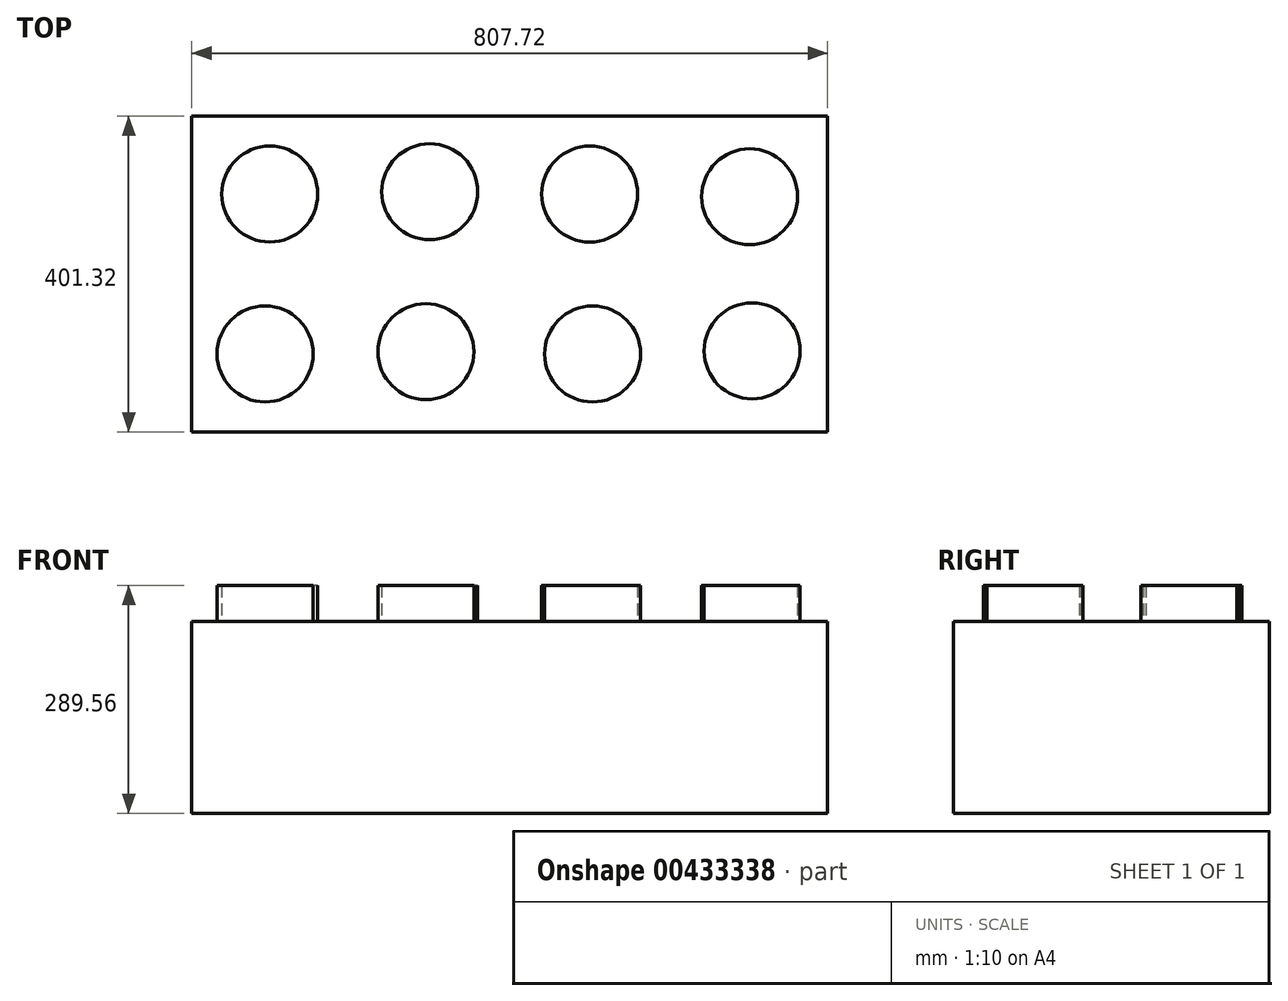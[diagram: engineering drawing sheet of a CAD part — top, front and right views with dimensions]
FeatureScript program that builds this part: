
annotation { "Feature Type Name" : "Feature", "Feature Type Description" : "" }
export const myFeature = defineFeature(function(context is Context, id is Id, definition is map)
    precondition{}
    {
        {
            var Q0;
            Q0=qCreatedBy(makeId("Top.planeOp"),FACE);
            var sketch = newSketch(context, id + "F0", { "sketchPlane" : qUnion([Q0])});
            skLineSegment(sketch, "E0.bottom", {"start": v(-391.6, 82.43) * mm, "end": v(416.12, 82.43) * mm});
            skLineSegment(sketch, "E0.top", {"start": v(-391.6, -318.9) * mm, "end": v(416.12, -318.9) * mm});
            skLineSegment(sketch, "E0.left", {"start": v(-391.6, 82.43) * mm, "end": v(-391.6, -318.9) * mm});
            skLineSegment(sketch, "E0.right", {"start": v(416.12, 82.43) * mm, "end": v(416.12, -318.9) * mm});
            skSolve(sketch);
        }
        {
            var Q0;
            Q0 = qSketchRegion(id + "F0", true);
            extrude(context, id + "F1", {"entities" : qUnion([Q0]), "depth" : 243.84 * mm});
        }
        {
            var Q0;
            Q0=makeQuery(id+"F1.opExtrude","CAP_FACE",FACE,{"disambiguationData":[OSD([sQuery(id+"F0.wireOp",EDGE,"E0.bottom"),sQuery(id+"F0.wireOp",EDGE,"E0.top"),sQuery(id+"F0.wireOp",EDGE,"E0.left"),sQuery(id+"F0.wireOp",EDGE,"E0.right")])],"isStart":false});
            var sketch = newSketch(context, id + "F2", { "sketchPlane" : qUnion([Q0])});
            skCircle(sketch, "E1", {"center": v(-292.54, -16.63) * mm, "radius": 60.96 * mm});
            skCircle(sketch, "E2", {"center": v(-89.34, -13.7) * mm, "radius": 60.96 * mm});
            skCircle(sketch, "E3", {"center": v(113.84, -16.64) * mm, "radius": 60.96 * mm});
            skCircle(sketch, "E4", {"center": v(317.01, -19.95) * mm, "radius": 60.96 * mm});
            skCircle(sketch, "E5", {"center": v(-298.57, -219.74) * mm, "radius": 60.96 * mm});
            skCircle(sketch, "E6", {"center": v(-94.25, -216.9) * mm, "radius": 60.96 * mm});
            skCircle(sketch, "E7", {"center": v(117.44, -219.8) * mm, "radius": 60.96 * mm});
            skCircle(sketch, "E8", {"center": v(320.06, -215.88) * mm, "radius": 60.96 * mm});
            skSolve(sketch);
        }
        {
            var Q0;
            Q0=makeQuery(id+"F2.imprint","IMPRINT",FACE,{"disambiguationData":[TD([[makeQuery(id+"F2.imprint","IMPRINT",EDGE,{"derivedFrom":sQuery(id+"F2.wireOp",EDGE,"E3")}),1.0]])]});
            var Q1;
            Q1=makeQuery(id+"F2.imprint","IMPRINT",FACE,{"disambiguationData":[TD([[makeQuery(id+"F2.imprint","IMPRINT",EDGE,{"derivedFrom":sQuery(id+"F2.wireOp",EDGE,"E4")}),1.0]])]});
            var Q2;
            Q2=makeQuery(id+"F2.imprint","IMPRINT",FACE,{"disambiguationData":[TD([[makeQuery(id+"F2.imprint","IMPRINT",EDGE,{"derivedFrom":sQuery(id+"F2.wireOp",EDGE,"E5")}),1.0]])]});
            var Q3;
            Q3=makeQuery(id+"F2.imprint","IMPRINT",FACE,{"disambiguationData":[TD([[makeQuery(id+"F2.imprint","IMPRINT",EDGE,{"derivedFrom":sQuery(id+"F2.wireOp",EDGE,"E6")}),1.0]])]});
            var Q4;
            Q4=makeQuery(id+"F2.imprint","IMPRINT",FACE,{"disambiguationData":[TD([[makeQuery(id+"F2.imprint","IMPRINT",EDGE,{"derivedFrom":sQuery(id+"F2.wireOp",EDGE,"E7")}),1.0]])]});
            var Q5;
            Q5=makeQuery(id+"F2.imprint","IMPRINT",FACE,{"disambiguationData":[TD([[makeQuery(id+"F2.imprint","IMPRINT",EDGE,{"derivedFrom":sQuery(id+"F2.wireOp",EDGE,"E8")}),1.0]])]});
            var Q6;
            Q6=makeQuery(id+"F2.imprint","IMPRINT",FACE,{"disambiguationData":[TD([[makeQuery(id+"F2.imprint","IMPRINT",EDGE,{"derivedFrom":sQuery(id+"F2.wireOp",EDGE,"E2")}),1.0]])]});
            var Q7;
            Q7=makeQuery(id+"F2.imprint","IMPRINT",FACE,{"disambiguationData":[TD([[makeQuery(id+"F2.imprint","IMPRINT",EDGE,{"derivedFrom":sQuery(id+"F2.wireOp",EDGE,"E1")}),1.0]])]});
            extrude(context, id + "F3", {"entities" : qUnion([Q0, Q1, Q2, Q3, Q4, Q5, Q6, Q7]), "operationType" : NewBodyOperationType.ADD, "depth" : 45.72 * mm});
        }
        {
            var Q0;
            Q0=qCreatedBy(makeId("Top.planeOp"),FACE);
            var sketch = newSketch(context, id + "F4", { "sketchPlane" : qUnion([Q0])});
            skLineSegment(sketch, "E9.bottom", {"start": v(-361.12, -288.41) * mm, "end": v(385.64, -288.41) * mm});
            skLineSegment(sketch, "E9.top", {"start": v(-361.12, 51.95) * mm, "end": v(385.64, 51.95) * mm});
            skLineSegment(sketch, "E9.left", {"start": v(-361.12, -288.41) * mm, "end": v(-361.12, 51.95) * mm});
            skLineSegment(sketch, "E9.right", {"start": v(385.64, -288.41) * mm, "end": v(385.64, 51.95) * mm});
            skCircle(sketch, "E10", {"center": v(-208.45, -102.04) * mm, "radius": 82.55 * mm});
            skCircle(sketch, "E11", {"center": v(27.99, -95.27) * mm, "radius": 82.55 * mm});
            skCircle(sketch, "E12", {"center": v(240.39, -99.76) * mm, "radius": 82.55 * mm});
            skCircle(sketch, "E13", {"center": v(-208.45, -102.04) * mm, "radius": 60.96 * mm});
            skCircle(sketch, "E14", {"center": v(27.99, -95.27) * mm, "radius": 60.96 * mm});
            skCircle(sketch, "E15", {"center": v(240.39, -99.76) * mm, "radius": 60.96 * mm});
            skSolve(sketch);
        }
        {
            var Q0;
            Q0 = qSketchRegion(id + "F4", true);
            var Q1;
            Q1=makeQuery(id+"F4.imprint","IMPRINT",FACE,{"disambiguationData":[TD([[makeQuery(id+"F4.imprint","IMPRINT",EDGE,{"derivedFrom":sQuery(id+"F4.wireOp",EDGE,"E13")}),1.0]])]});
            var Q2;
            Q2=makeQuery(id+"F4.imprint","IMPRINT",FACE,{"disambiguationData":[TD([[makeQuery(id+"F4.imprint","IMPRINT",EDGE,{"derivedFrom":sQuery(id+"F4.wireOp",EDGE,"E14")}),1.0]])]});
            var Q3;
            Q3=makeQuery(id+"F4.imprint","IMPRINT",FACE,{"disambiguationData":[TD([[makeQuery(id+"F4.imprint","IMPRINT",EDGE,{"derivedFrom":sQuery(id+"F4.wireOp",EDGE,"E15")}),1.0]])]});
            extrude(context, id + "F5", {"entities" : qUnion([Q0, Q1, Q2, Q3]), "operationType" : NewBodyOperationType.ADD, "depth" : 45.72 * mm});
        }
    });
